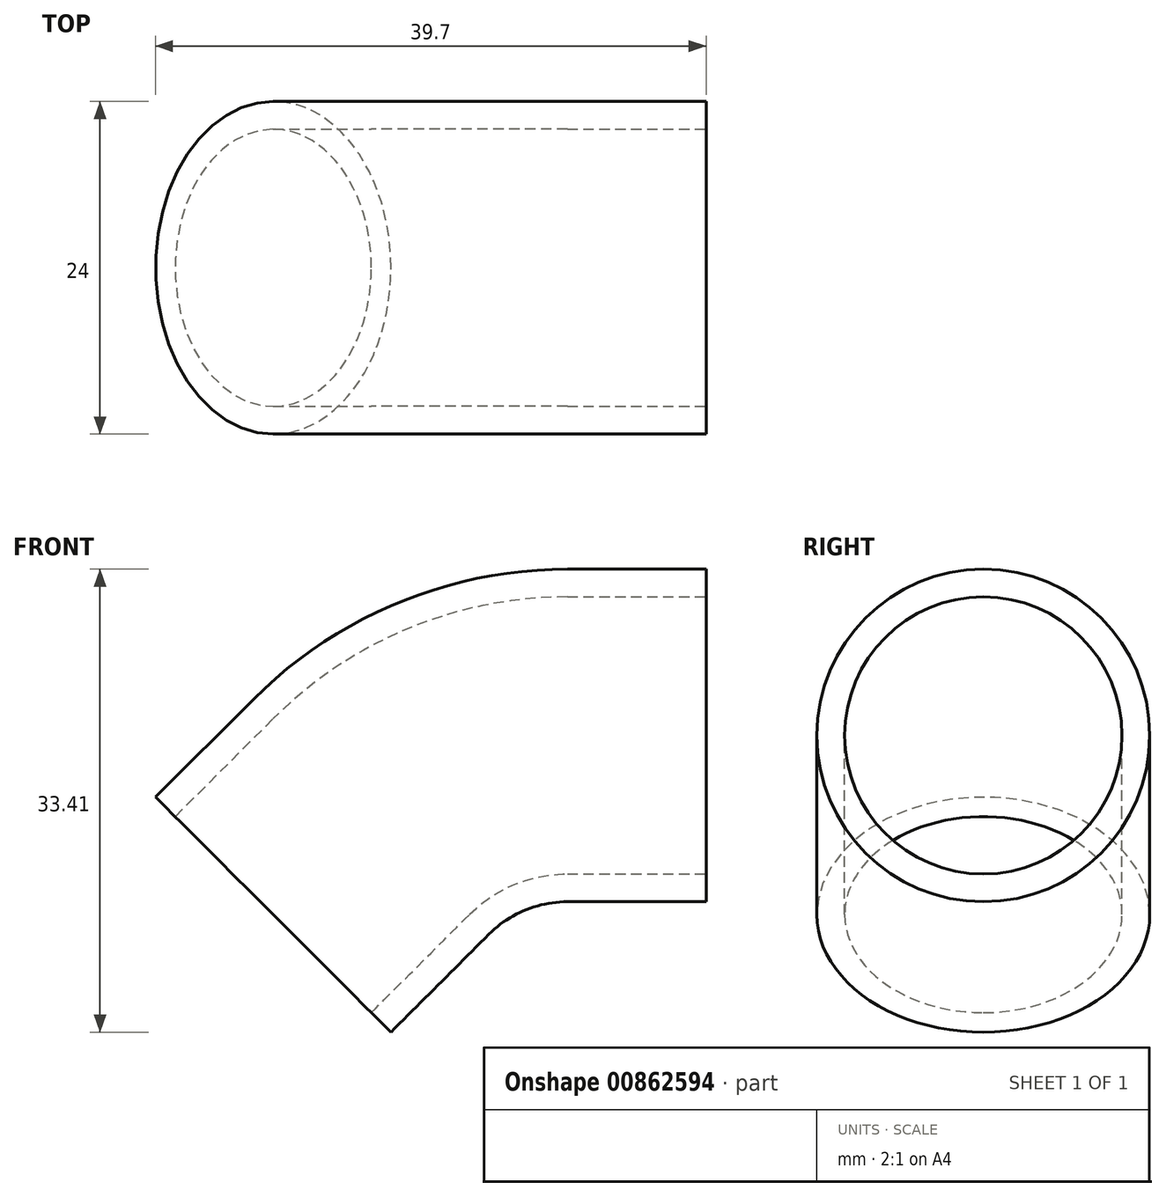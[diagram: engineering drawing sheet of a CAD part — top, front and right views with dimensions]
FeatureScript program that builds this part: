
annotation { "Feature Type Name" : "Feature", "Feature Type Description" : "" }
export const myFeature = defineFeature(function(context is Context, id is Id, definition is map)
    precondition{}
    {
        {
            var Q0;
            Q0=qCreatedBy(makeId("Front.planeOp"),FACE);
            var sketch = newSketch(context, id + "F0", { "sketchPlane" : qUnion([Q0])});
            skLineSegment(sketch, "E0", {"start": v(0, 0) * mm, "end": v(-10, 0) * mm});
            skArc(sketch, "E1.filletArc", {"start": v(-10, 0) * mm, "mid": v(-17.65, -1.52) * mm, "end": v(-24.14, -5.86) * mm});
            skLineSegment(sketch, "E2", {"start": v(-24.14, -5.86) * mm, "end": v(-31.21, -12.93) * mm});
            skSolve(sketch);
        }
        {
            var Q0;
            Q0=qCreatedBy(makeId("Right.planeOp"),FACE);
            var sketch = newSketch(context, id + "F1", { "sketchPlane" : qUnion([Q0])});
            skCircle(sketch, "E3", {"center": v(0, 0) * mm, "radius": 12 * mm});
            skCircle(sketch, "E4.0", {"center": v(0, 0) * mm, "radius": 10 * mm});
            skSolve(sketch);
        }
        {
            var Q0;
            Q0=makeQuery(id+"F1.imprint","IMPRINT",FACE,{"disambiguationData":[TD([[makeQuery(id+"F1.imprint","IMPRINT",EDGE,{"derivedFrom":sQuery(id+"F1.wireOp",EDGE,"E3")}),1.0]])]});
            var Q1;
            Q1=qSketchRegion(id+"F0",true);
            var Q2;
            Q2=sQuery(id+"F0.wireOp",EDGE,"E0");
            var Q3;
            Q3=sQuery(id+"F0.wireOp",EDGE,"E1.filletArc");
            var Q4;
            Q4=sQuery(id+"F0.wireOp",EDGE,"E2");
            sweep(context, id + "F2", {"profiles" : qUnion([Q0, Q1]), "path" : qUnion([Q2, Q3, Q4])});
        }
    });
